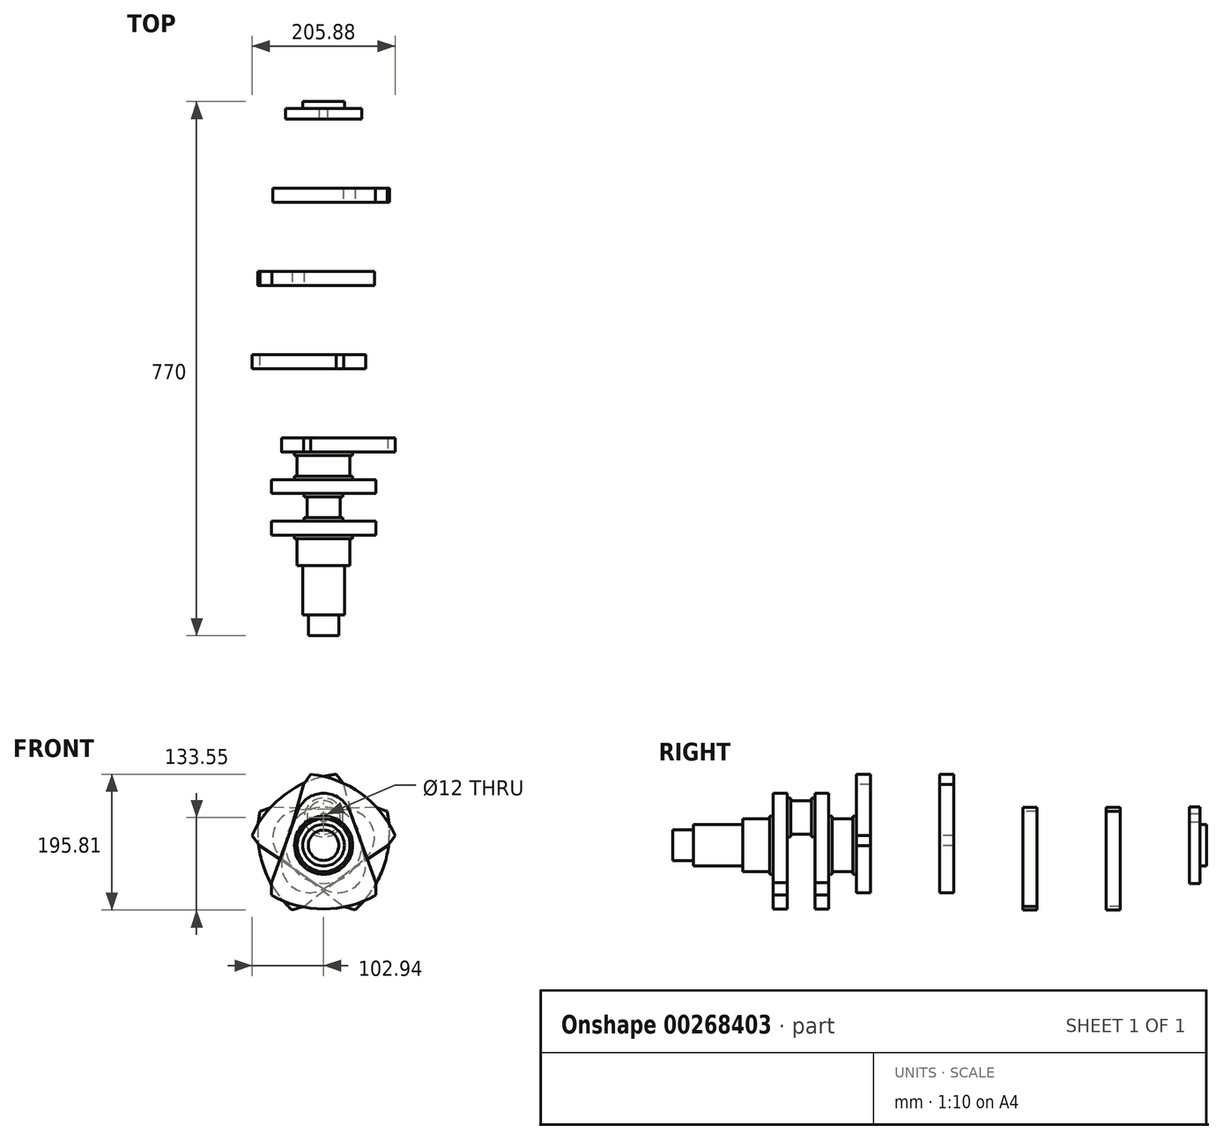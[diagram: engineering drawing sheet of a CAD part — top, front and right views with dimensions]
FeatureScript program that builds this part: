
annotation { "Feature Type Name" : "Feature", "Feature Type Description" : "" }
export const myFeature = defineFeature(function(context is Context, id is Id, definition is map)
    precondition{}
    {
        {
            assignVariable(context, id + "F0", {"name" : "wangen_breite", "anyValue" : 20});
        }
        {
            assignVariable(context, id + "F1", {"name" : "lager_klein_breite", "anyValue" : 40});
        }
        {
            assignVariable(context, id + "F2", {"name" : "lager_gross_breite", "anyValue" : 40});
        }
        {
            assignVariable(context, id + "F3", {"name" : "pleuel_breite", "anyValue" : 2 * getVariable(context, 'wangen_breite') + getVariable(context, 'lager_gross_breite') + getVariable(context, 'lager_klein_breite')});
        }
        {
            var Q0;
            Q0=qCreatedBy(makeId("Front.planeOp"),FACE);
            var sketch = newSketch(context, id + "F4", { "sketchPlane" : qUnion([Q0])});
            skLineSegment(sketch, "E0", {"start": v(-37.59, 48.68) * mm, "end": v(-75, -54.1) * mm});
            skLineSegment(sketch, "E1", {"start": v(-75, -54.1) * mm, "end": v(-75, -71.9) * mm});
            skLineSegment(sketch, "E2", {"start": v(75, -71.9) * mm, "end": v(75, -54.1) * mm});
            skLineSegment(sketch, "E3", {"start": v(75, -54.1) * mm, "end": v(37.59, 48.68) * mm});
            skArc(sketch, "E4", {"start": v(37.59, 48.68) * mm, "mid": v(0, 75) * mm, "end": v(-37.59, 48.68) * mm});
            skArc(sketch, "E5", {"start": v(-75, -71.9) * mm, "mid": v(0, -92) * mm, "end": v(75, -71.9) * mm});
            skSolve(sketch);
        }
        {
            var Q0;
            Q0 = qSketchRegion(id + "F4", true);
            extrude(context, id + "F5", {"entities" : qUnion([Q0]), "oppositeDirection" : true, "depth" : (getVariable(context, 'wangen_breite')) * mm});
        }
        {
            var Q0;
            Q0=qCreatedBy(makeId("Right.planeOp"),FACE);
            var sketch = newSketch(context, id + "F6", { "sketchPlane" : qUnion([Q0])});
            skLineSegment(sketch, "E6", {"start": v(0, 0) * mm, "end": v(0, 28) * mm});
            skLineSegment(sketch, "E7", {"start": v(0, 28) * mm, "end": v(5, 28) * mm});
            skLineSegment(sketch, "E8", {"start": v(5, 28) * mm, "end": v(5, 24) * mm});
            skLineSegment(sketch, "E9", {"start": v(5, 24) * mm, "end": v(35, 24) * mm});
            skLineSegment(sketch, "E10", {"start": v(35, 24) * mm, "end": v(35, 28) * mm});
            skLineSegment(sketch, "E11", {"start": v(35, 28) * mm, "end": v(40, 28) * mm});
            skLineSegment(sketch, "E12", {"start": v(40, 28) * mm, "end": v(40, 0) * mm});
            skLineSegment(sketch, "E13", {"start": v(40, 0) * mm, "end": v(0, 0) * mm});
            skSolve(sketch);
        }
        {
            var Q0;
            Q0 = qSketchRegion(id + "F6", true);
            var Q1;
            Q1=sQuery(id+"F6.wireOp",EDGE,"E13");
            revolve(context, id + "F7", {"entities" : qUnion([Q0]), "axis" : qUnion([Q1]), "revolveType" : RevolveType.FULL});
        }
        {
            var Q0;
            Q0=qCreatedBy(makeId("Right.planeOp"),FACE);
            var sketch = newSketch(context, id + "F8", { "sketchPlane" : qUnion([Q0])});
            skLineSegment(sketch, "E14", {"start": v(0, 0) * mm, "end": v(0, 42) * mm});
            skLineSegment(sketch, "E15", {"start": v(0, 42) * mm, "end": v(5, 42) * mm});
            skLineSegment(sketch, "E16", {"start": v(5, 42) * mm, "end": v(5, 38) * mm});
            skLineSegment(sketch, "E17", {"start": v(5, 38) * mm, "end": v(35, 38) * mm});
            skLineSegment(sketch, "E18", {"start": v(35, 38) * mm, "end": v(35, 42) * mm});
            skLineSegment(sketch, "E19", {"start": v(35, 42) * mm, "end": v(40, 42) * mm});
            skLineSegment(sketch, "E20", {"start": v(40, 42) * mm, "end": v(40, 0) * mm});
            skLineSegment(sketch, "E21", {"start": v(40, 0) * mm, "end": v(0, 0) * mm});
            skSolve(sketch);
        }
        {
            var Q0;
            Q0 = qSketchRegion(id + "F8", true);
            var Q1;
            Q1=sQuery(id+"F8.wireOp",EDGE,"E21");
            revolve(context, id + "F9", {"entities" : qUnion([Q0]), "axis" : qUnion([Q1]), "revolveType" : RevolveType.FULL});
        }
        {
            var Q0;
            Q0=makeQuery(id+"F5.opExtrude","SWEPT_BODY",BODY,{"disambiguationData":[OSD([sQuery(id+"F4.wireOp",EDGE,"E0"),sQuery(id+"F4.wireOp",EDGE,"E1"),sQuery(id+"F4.wireOp",EDGE,"E2"),sQuery(id+"F4.wireOp",EDGE,"E3"),sQuery(id+"F4.wireOp",EDGE,"E4"),sQuery(id+"F4.wireOp",EDGE,"E5")])]});
            var Q1;
            Q1=qCreatedBy(makeId("Front.planeOp"),FACE);
            transform(context, id + "F10", {"entities" : qUnion([Q0]), "transformType" : TransformType.TRANSLATION_DISTANCE, "transformDirection" : qUnion([Q1]), "distance" : (getVariable(context, 'wangen_breite') + getVariable(context, 'lager_klein_breite')) * mm, "oppositeDirection" : true, "makeCopy" : true});
        }
        {
            var Q0;
            Q0=makeQuery(id+"F7.opRevolve","SWEPT_BODY",BODY,{"disambiguationData":[OSD([sQuery(id+"F6.wireOp",EDGE,"E6"),sQuery(id+"F6.wireOp",EDGE,"E7"),sQuery(id+"F6.wireOp",EDGE,"E8"),sQuery(id+"F6.wireOp",EDGE,"E9"),sQuery(id+"F6.wireOp",EDGE,"E10"),sQuery(id+"F6.wireOp",EDGE,"E11"),sQuery(id+"F6.wireOp",EDGE,"E12"),sQuery(id+"F6.wireOp",EDGE,"E13")])]});
            var Q1;
            Q1=qCreatedBy(makeId("Top.planeOp"),FACE);
            transform(context, id + "F11", {"entities" : qUnion([Q0]), "transformType" : TransformType.TRANSLATION_DISTANCE, "transformDirection" : qUnion([Q1]), "distance" : 40 * mm, "makeCopy" : false});
        }
        {
            var Q0;
            Q0=makeQuery(id+"F7.opRevolve","SWEPT_BODY",BODY,{"disambiguationData":[OSD([sQuery(id+"F6.wireOp",EDGE,"E6"),sQuery(id+"F6.wireOp",EDGE,"E7"),sQuery(id+"F6.wireOp",EDGE,"E8"),sQuery(id+"F6.wireOp",EDGE,"E9"),sQuery(id+"F6.wireOp",EDGE,"E10"),sQuery(id+"F6.wireOp",EDGE,"E11"),sQuery(id+"F6.wireOp",EDGE,"E12"),sQuery(id+"F6.wireOp",EDGE,"E13")])]});
            var Q1;
            Q1=qCreatedBy(makeId("Front.planeOp"),FACE);
            transform(context, id + "F12", {"entities" : qUnion([Q0]), "transformType" : TransformType.TRANSLATION_DISTANCE, "transformDirection" : qUnion([Q1]), "distance" : (getVariable(context, 'wangen_breite')) * mm, "oppositeDirection" : true, "makeCopy" : false});
        }
        {
            var Q0;
            Q0=makeQuery(id+"F9.opRevolve","SWEPT_BODY",BODY,{"disambiguationData":[OSD([sQuery(id+"F8.wireOp",EDGE,"E14"),sQuery(id+"F8.wireOp",EDGE,"E15"),sQuery(id+"F8.wireOp",EDGE,"E16"),sQuery(id+"F8.wireOp",EDGE,"E17"),sQuery(id+"F8.wireOp",EDGE,"E18"),sQuery(id+"F8.wireOp",EDGE,"E19"),sQuery(id+"F8.wireOp",EDGE,"E20"),sQuery(id+"F8.wireOp",EDGE,"E21")])]});
            var Q1;
            Q1=qCreatedBy(makeId("Front.planeOp"),FACE);
            transform(context, id + "F13", {"entities" : qUnion([Q0]), "transformType" : TransformType.TRANSLATION_DISTANCE, "transformDirection" : qUnion([Q1]), "distance" : (2 * (getVariable(context, 'wangen_breite')) + getVariable(context, 'lager_klein_breite')) * mm, "oppositeDirection" : true, "makeCopy" : false});
        }
        {
            var Q0;
            Q0=makeQuery(id+"F5.opExtrude","SWEPT_BODY",BODY,{"disambiguationData":[OSD([sQuery(id+"F4.wireOp",EDGE,"E0"),sQuery(id+"F4.wireOp",EDGE,"E1"),sQuery(id+"F4.wireOp",EDGE,"E2"),sQuery(id+"F4.wireOp",EDGE,"E3"),sQuery(id+"F4.wireOp",EDGE,"E4"),sQuery(id+"F4.wireOp",EDGE,"E5")])]});
            var Q1;
            Q1=qCreatedBy(makeId("Front.planeOp"),FACE);
            transform(context, id + "F14", {"entities" : qUnion([Q0]), "transformType" : TransformType.TRANSLATION_DISTANCE, "transformDirection" : qUnion([Q1]), "distance" : (getVariable(context, 'pleuel_breite')) * mm, "oppositeDirection" : true, "makeCopy" : true});
        }
        {
            var Q0;
            Q0=makeQuery(id+"F5.opExtrude","SWEPT_BODY",BODY,{"disambiguationData":[OSD([sQuery(id+"F4.wireOp",EDGE,"E0"),sQuery(id+"F4.wireOp",EDGE,"E1"),sQuery(id+"F4.wireOp",EDGE,"E2"),sQuery(id+"F4.wireOp",EDGE,"E3"),sQuery(id+"F4.wireOp",EDGE,"E4"),sQuery(id+"F4.wireOp",EDGE,"E5")])]});
            var Q1;
            Q1=qCreatedBy(makeId("Front.planeOp"),FACE);
            transform(context, id + "F15", {"entities" : qUnion([Q0]), "transformType" : TransformType.TRANSLATION_DISTANCE, "transformDirection" : qUnion([Q1]), "distance" : (2 * getVariable(context, 'pleuel_breite')) * mm, "oppositeDirection" : true, "makeCopy" : true});
        }
        {
            var Q0;
            Q0=makeQuery(id+"F5.opExtrude","SWEPT_BODY",BODY,{"disambiguationData":[OSD([sQuery(id+"F4.wireOp",EDGE,"E0"),sQuery(id+"F4.wireOp",EDGE,"E1"),sQuery(id+"F4.wireOp",EDGE,"E2"),sQuery(id+"F4.wireOp",EDGE,"E3"),sQuery(id+"F4.wireOp",EDGE,"E4"),sQuery(id+"F4.wireOp",EDGE,"E5")])]});
            var Q1;
            Q1=qCreatedBy(makeId("Front.planeOp"),FACE);
            transform(context, id + "F16", {"entities" : qUnion([Q0]), "transformType" : TransformType.TRANSLATION_DISTANCE, "transformDirection" : qUnion([Q1]), "distance" : (3 * getVariable(context, 'pleuel_breite')) * mm, "oppositeDirection" : true, "makeCopy" : true});
        }
        {
            var Q0;
            Q0=makeQuery(id+"F5.opExtrude","SWEPT_BODY",BODY,{"disambiguationData":[OSD([sQuery(id+"F4.wireOp",EDGE,"E0"),sQuery(id+"F4.wireOp",EDGE,"E1"),sQuery(id+"F4.wireOp",EDGE,"E2"),sQuery(id+"F4.wireOp",EDGE,"E3"),sQuery(id+"F4.wireOp",EDGE,"E4"),sQuery(id+"F4.wireOp",EDGE,"E5")])]});
            var Q1;
            Q1=qCreatedBy(makeId("Front.planeOp"),FACE);
            transform(context, id + "F17", {"entities" : qUnion([Q0]), "transformType" : TransformType.TRANSLATION_DISTANCE, "transformDirection" : qUnion([Q1]), "distance" : (4 * getVariable(context, 'pleuel_breite')) * mm, "oppositeDirection" : true, "makeCopy" : true});
        }
        {
            var Q0;
            Q0=makeQuery(id+"F17.opPattern","COPY",BODY,{"derivedFrom":makeQuery(id+"F5.opExtrude","SWEPT_BODY",BODY,{"disambiguationData":[OSD([sQuery(id+"F4.wireOp",EDGE,"E0"),sQuery(id+"F4.wireOp",EDGE,"E1"),sQuery(id+"F4.wireOp",EDGE,"E2"),sQuery(id+"F4.wireOp",EDGE,"E3"),sQuery(id+"F4.wireOp",EDGE,"E4"),sQuery(id+"F4.wireOp",EDGE,"E5")])]}),"instanceName":"1"});
            var Q1;
            Q1=makeQuery(id+"F9.opRevolve","SWEPT_FACE",FACE,{"disambiguationData":[OSD([sQuery(id+"F8.wireOp",EDGE,"E17")])]});
            transform(context, id + "F18", {"entities" : qUnion([Q0]), "transformType" : TransformType.ROTATION, "transformAxis" : qUnion([Q1]), "angle" : 72 * degree, "oppositeDirection" : true, "makeCopy" : false});
        }
        {
            var Q0;
            Q0=makeQuery(id+"F16.opPattern","COPY",BODY,{"derivedFrom":makeQuery(id+"F5.opExtrude","SWEPT_BODY",BODY,{"disambiguationData":[OSD([sQuery(id+"F4.wireOp",EDGE,"E0"),sQuery(id+"F4.wireOp",EDGE,"E1"),sQuery(id+"F4.wireOp",EDGE,"E2"),sQuery(id+"F4.wireOp",EDGE,"E3"),sQuery(id+"F4.wireOp",EDGE,"E4"),sQuery(id+"F4.wireOp",EDGE,"E5")])]}),"instanceName":"1"});
            var Q1;
            Q1=makeQuery(id+"F9.opRevolve","SWEPT_FACE",FACE,{"disambiguationData":[OSD([sQuery(id+"F8.wireOp",EDGE,"E17")])]});
            transform(context, id + "F19", {"entities" : qUnion([Q0]), "transformType" : TransformType.ROTATION, "transformAxis" : qUnion([Q1]), "angle" : 288 * degree, "oppositeDirection" : true, "makeCopy" : false});
        }
        {
            var Q0;
            Q0=makeQuery(id+"F15.opPattern","COPY",BODY,{"derivedFrom":makeQuery(id+"F5.opExtrude","SWEPT_BODY",BODY,{"disambiguationData":[OSD([sQuery(id+"F4.wireOp",EDGE,"E0"),sQuery(id+"F4.wireOp",EDGE,"E1"),sQuery(id+"F4.wireOp",EDGE,"E2"),sQuery(id+"F4.wireOp",EDGE,"E3"),sQuery(id+"F4.wireOp",EDGE,"E4"),sQuery(id+"F4.wireOp",EDGE,"E5")])]}),"instanceName":"1"});
            var Q1;
            Q1=makeQuery(id+"F9.opRevolve","SWEPT_FACE",FACE,{"disambiguationData":[OSD([sQuery(id+"F8.wireOp",EDGE,"E17")])]});
            transform(context, id + "F20", {"entities" : qUnion([Q0]), "transformType" : TransformType.ROTATION, "transformAxis" : qUnion([Q1]), "angle" : 216 * degree, "oppositeDirection" : true, "makeCopy" : false});
        }
        {
            var Q0;
            Q0=makeQuery(id+"F14.opPattern","COPY",BODY,{"derivedFrom":makeQuery(id+"F5.opExtrude","SWEPT_BODY",BODY,{"disambiguationData":[OSD([sQuery(id+"F4.wireOp",EDGE,"E0"),sQuery(id+"F4.wireOp",EDGE,"E1"),sQuery(id+"F4.wireOp",EDGE,"E2"),sQuery(id+"F4.wireOp",EDGE,"E3"),sQuery(id+"F4.wireOp",EDGE,"E4"),sQuery(id+"F4.wireOp",EDGE,"E5")])]}),"instanceName":"1"});
            var Q1;
            Q1=makeQuery(id+"F9.opRevolve","SWEPT_FACE",FACE,{"disambiguationData":[OSD([sQuery(id+"F8.wireOp",EDGE,"E17")])]});
            transform(context, id + "F21", {"entities" : qUnion([Q0]), "transformType" : TransformType.ROTATION, "transformAxis" : qUnion([Q1]), "angle" : 144 * degree, "oppositeDirection" : true, "makeCopy" : false});
        }
        {
            var Q0;
            Q0=qCreatedBy(makeId("Right.planeOp"),FACE);
            var sketch = newSketch(context, id + "F22", { "sketchPlane" : qUnion([Q0])});
            skLineSegment(sketch, "E22", {"start": v(0, 0) * mm, "end": v(-145, 0) * mm});
            skLineSegment(sketch, "E23", {"start": v(-145, 0) * mm, "end": v(-145, 22) * mm});
            skLineSegment(sketch, "E24", {"start": v(-145, 22) * mm, "end": v(-115, 22) * mm});
            skLineSegment(sketch, "E25", {"start": v(-115, 22) * mm, "end": v(-115, 30) * mm});
            skLineSegment(sketch, "E26", {"start": v(-115, 30) * mm, "end": v(-44, 30) * mm});
            skLineSegment(sketch, "E27", {"start": v(-44, 30) * mm, "end": v(-44, 38) * mm});
            skLineSegment(sketch, "E28", {"start": v(-44, 38) * mm, "end": v(-5, 38) * mm});
            skLineSegment(sketch, "E29", {"start": v(-5, 38) * mm, "end": v(-5, 42) * mm});
            skLineSegment(sketch, "E30", {"start": v(-5, 42) * mm, "end": v(0, 42) * mm});
            skLineSegment(sketch, "E31", {"start": v(0, 42) * mm, "end": v(0, 0) * mm});
            skSolve(sketch);
        }
        {
            var Q0;
            Q0 = qSketchRegion(id + "F22", true);
            var Q1;
            Q1=sQuery(id+"F22.wireOp",EDGE,"E22");
            revolve(context, id + "F23", {"entities" : qUnion([Q0]), "axis" : qUnion([Q1]), "revolveType" : RevolveType.FULL});
        }
        {
            var Q0;
            Q0=qCreatedBy(makeId("Right.planeOp"),FACE);
            var sketch = newSketch(context, id + "F24", { "sketchPlane" : qUnion([Q0])});
            skLineSegment(sketch, "E32", {"start": v(0, 0) * mm, "end": v(0, 55) * mm});
            skLineSegment(sketch, "E33", {"start": v(0, 55) * mm, "end": v(15, 55) * mm});
            skLineSegment(sketch, "E34", {"start": v(15, 55) * mm, "end": v(15, 30) * mm});
            skLineSegment(sketch, "E35", {"start": v(15, 30) * mm, "end": v(25, 30) * mm});
            skLineSegment(sketch, "E36", {"start": v(25, 30) * mm, "end": v(25, 0) * mm});
            skLineSegment(sketch, "E37", {"start": v(25, 0) * mm, "end": v(0, 0) * mm});
            skSolve(sketch);
        }
        {
            var Q0;
            Q0=makeQuery(id+"F24.imprint","IMPRINT",FACE,{"disambiguationData":[TD([[makeQuery(id+"F24.imprint","IMPRINT",EDGE,{"derivedFrom":sQuery(id+"F24.wireOp",EDGE,"E32")}),-1.0]])]});
            var Q1;
            Q1=sQuery(id+"F24.wireOp",EDGE,"E37");
            revolve(context, id + "F25", {"entities" : qUnion([Q0]), "axis" : qUnion([Q1]), "revolveType" : RevolveType.FULL});
        }
        {
            var Q0;
            Q0=makeQuery(id+"F25.opRevolve","SWEPT_FACE",FACE,{"disambiguationData":[OSD([sQuery(id+"F24.wireOp",EDGE,"E34")])]});
            var sketch = newSketch(context, id + "F26", { "sketchPlane" : qUnion([Q0])});
            skPoint(sketch, "E38", {"position": v(0, 40) * mm});
            skSolve(sketch);
        }
        {
            var Q0;
            Q0=sQuery(id+"F26.wireOp",VERTEX,"E38");
            var Q1;
            Q1=makeQuery(id+"F25.opRevolve","SWEPT_BODY",BODY,{"disambiguationData":[OSD([sQuery(id+"F24.wireOp",EDGE,"E32"),sQuery(id+"F24.wireOp",EDGE,"E33"),sQuery(id+"F24.wireOp",EDGE,"E34"),sQuery(id+"F24.wireOp",EDGE,"E35"),sQuery(id+"F24.wireOp",EDGE,"E36"),sQuery(id+"F24.wireOp",EDGE,"E37")])]});
            hole(context, id + "F27", {"style" : HoleStyle.SIMPLE, "endStyle" : HoleEndStyle.THROUGH, "holeDiameter" : 12 * mm, "tappedDepth" : 12 * mm, "tapClearance" : 3, "locations" : qUnion([Q0]), "scope" : qUnion([Q1])});
        }
        {
            var Q0;
            Q0=makeQuery(id+"F25.opRevolve","SWEPT_BODY",BODY,{"disambiguationData":[OSD([sQuery(id+"F24.wireOp",EDGE,"E32"),sQuery(id+"F24.wireOp",EDGE,"E33"),sQuery(id+"F24.wireOp",EDGE,"E34"),sQuery(id+"F24.wireOp",EDGE,"E35"),sQuery(id+"F24.wireOp",EDGE,"E36"),sQuery(id+"F24.wireOp",EDGE,"E37")])]});
            var Q1;
            Q1=qCreatedBy(makeId("Front.planeOp"),FACE);
            transform(context, id + "F28", {"entities" : qUnion([Q0]), "transformType" : TransformType.TRANSLATION_DISTANCE, "transformDirection" : qUnion([Q1]), "distance" : (5 * getVariable(context, 'pleuel_breite')) * mm, "oppositeDirection" : true, "makeCopy" : false});
        }
    });
